# Revit family: HVAC_Heaters_Enertech_CTC-EcoHeat-400
name_source: partatom
category: Specialty Equipment
revit_build: Autodesk Revit 2017 (Build: 20190508_0315(x64)
units: mm (PartAtom-declared; Revit-internal decimal feet)

## family parameters
Always vertical = Yes
Cut with Voids When Loaded = No
OmniClass Number = 23.75.00.00
OmniClass Title = Climate Control (HVAC)
Part Type = Normal
Room Calculation Point = No
Round Connector Dimension = Use Diameter
Shared = No
Work Plane-Based = No

## types (12) — shared parameters
AssetType = Fixed
BIMObjectName = HVAC_Heaters_Enertech_CTC-EcoHeat-400
Brand = CTC
BrineSystem_Min_MaxPressure = 0.2-3.0 bar
Capacity = Fixed
Category = Heat pumps, Ground source
Color = White
ConvergoRefNr = 0091-1710-0011-SE
Description = CTC EcoHeat is a series of quiet, efficient on/off geothermal heat pumps with control touchscreen, hot water preparation and EnergyFlex, model 406-412, 6-12 kW, 230V-400V.
DurationUnit = Year
EnergyClass_HotWater_TapProfile = A/ L
HasProtectiveEarth = Yes
IP_Code = IP X1
IfcExportAs = IfcElectricalDeviceCommon
IfcExportType = HEATER
Manufacturer = Enertech AB
ManufacturerCountry = Sweden
ManufacturerName = Enertech AB
ManufacturerURL = https://ctc.se
Material = Steel/copper
MaxOperatingPressureHotWater = 10 bar
MaxOperatingPressureThermalStore = 3 bar
MinimumCeilingHeight = 1925 mm
NBSDescription = Air to water heat pumps
NBSReference = 90-40-40/320
Name = CTC-EcoHeat-400
NominalCurrent = 0 A
NominalDepth = 673 mm
NominalFrequencyRange = 50 Hz
NominalHeight = 1904 mm
NominalWidth = 596 mm
PhaseAngle = 0.00°
PowerFactor = 0 W
ProductInformation = CTC EcoHeat is a series of quiet, efficient on/off geothermal heat pumps with control touchscreen, hot water preparation and EnergyFlex, model 406-412, 6-12 kW, 230V-400V.
PumpMainMaterial = Stainless Steel
RefrigerantType = R407C
Revision = 4
Shape = Rectangular
Size = 673x596x1904 mm
Touchscreen = yes
UNSPSCCode = 40101806
URL = https://ctc-heating.com
Uniclass2 = Pr_40_70_65
Uniclass2015Description = Preparation catering equipment
Uniclass2015Reference = Pr_40_70_65
UsageCurrent = 0 A
Version = 1
VersionDate = 10/11/2020
WarrantyDurationUnit = Year
WaterVolumeHeathingSystem = 223 liters
WaterVolumeWaterSuply = 5.7 liters
zero-valued in all types: Cost

## per-type parameters (varying)
- CTC EcoHeat 406 - 400V3N: CO2Equivalent=3.370 tonnes; COP=4.57 kW; EANNumber=7333077000240; ElectricalDeviceNominalPower=9000 W; EnergyClassHeatingWithControl=A++/A+; EnergyClassHeatingWithoutControl=A++/A+; GroupFuse=10 A; HotTapWaterPerformance=173 liters; InPutPower=1.29 kW; MaxStartingCurrent=16.60 A; Model=CTC EcoHeat 406; ModelNumber=586610001; NominalVoltage=400 V; NumberOfPoles=3; OutputRangeIimmersionHeater=0.3-9.0 kW; RatedCurrent=12 A; RatedHeatOutputModerate=7 kW; RatedVoltage=1200 V; RefrigerantQuantity=1.9 kg; SCOPCold=4.3; SCOPModerate=4.3; SCOPWarm=4.1; Sound pressureLPA 1m=38 dB; SoundPowerLWA=43 dB; SpecifiedOutput=5.90 kW; Weight=273 kg
- CTC EcoHeat 408 - 400V3N: CO2Equivalent=3.370 tonnes; COP=4.58 kW; EANNumber=7333077000257; ElectricalDeviceNominalPower=9000 W; EnergyClassHeatingWithControl=A++/A++; EnergyClassHeatingWithoutControl=A++/A++; GroupFuse=10 A; HotTapWaterPerformance=173 liters; InPutPower=1.79 kW; MaxStartingCurrent=17.70 A; Model=CTC EcoHeat 408; ModelNumber=586610002; NominalVoltage=400 V; NumberOfPoles=3; OutputRangeIimmersionHeater=0.3-9.0 kW; RatedCurrent=13 A; RatedHeatOutputModerate=9 kW; RatedVoltage=1200 V; RefrigerantQuantity=1.9 kg; SCOPCold=4.2; SCOPModerate=4.2; SCOPWarm=4.1; Sound pressureLPA 1m=41 dB; SoundPowerLWA=46 dB; SpecifiedOutput=8.19 kW; Weight=274 kg
- CTC EcoHeat 410 - 400V3N: CO2Equivalent=3.370 tonnes; COP=4.60 kW; EANNumber=7333077000264; ElectricalDeviceNominalPower=9000 W; EnergyClassHeatingWithControl=A++/A++; EnergyClassHeatingWithoutControl=A++/A++; GroupFuse=10 A; HotTapWaterPerformance=173 liters; InPutPower=2.17 kW; MaxStartingCurrent=19.80 A; Model=CTC EcoHeat 410; ModelNumber=586610003; NominalVoltage=400 V; NumberOfPoles=3; OutputRangeIimmersionHeater=0.3-9.0 kW; RatedCurrent=13 A; RatedHeatOutputModerate=12 kW; RatedVoltage=1200 V; RefrigerantQuantity=1.9 kg; SCOPCold=4.2; SCOPModerate=4.1; SCOPWarm=4.0; Sound pressureLPA 1m=44 dB; SoundPowerLWA=49 dB; SpecifiedOutput=9.97 kW; Weight=278 kg
- CTC EcoHeat 412 - 400V3N: CO2Equivalent=4.080 tonnes; COP=4.60 kW; EANNumber=7333077000271; ElectricalDeviceNominalPower=9000 W; EnergyClassHeatingWithControl=A++/A++; EnergyClassHeatingWithoutControl=A++/A+; GroupFuse=16 A; HotTapWaterPerformance=173 liters; InPutPower=2.55 kW; MaxStartingCurrent=23.50 A; Model=CTC EcoHeat 412; ModelNumber=586610004; NominalVoltage=400 V; NumberOfPoles=3; OutputRangeIimmersionHeater=0.3-9.0 kW; RatedCurrent=14 A; RatedHeatOutputModerate=13 kW; RatedVoltage=1200 V; RefrigerantQuantity=2.3 kg; SCOPCold=4.1; SCOPModerate=4.1; SCOPWarm=4.0; Sound pressureLPA 1m=45 dB; SoundPowerLWA=50 dB; SpecifiedOutput=11.75 kW; Weight=291 kg
- CTC EcoHeat 406 - 230V1N: CO2Equivalent=3.370 tonnes; COP=4.57 kW; EANNumber=7333077000288; ElectricalDeviceNominalPower=9000 W; EnergyClassHeatingWithControl=A++/A+; EnergyClassHeatingWithoutControl=A++/A+; GroupFuse=16 A; HotTapWaterPerformance=173 liters; InPutPower=1.29 kW; MaxStartingCurrent=30 A; Model=CTC EcoHeat 406; ModelNumber=586611001; NominalVoltage=230 V; NumberOfPoles=1; OutputRangeIimmersionHeater=0.3-9.0 kW; RatedCurrent=52 A; RatedHeatOutputModerate=7 kW; RatedVoltage=230 V; RefrigerantQuantity=1.9 kg; SCOPCold=4.3; SCOPModerate=4.3; SCOPWarm=4.1; Sound pressureLPA 1m=38 dB; SoundPowerLWA=43 dB; SpecifiedOutput=5.90 kW; Weight=282 kg
- CTC EcoHeat 408 - 230V1N: CO2Equivalent=3.370 tonnes; COP=4.58 kW; EANNumber=7333077000295; ElectricalDeviceNominalPower=9000 W; EnergyClassHeatingWithControl=A++/A++; EnergyClassHeatingWithoutControl=A++/A++; GroupFuse=20 A; HotTapWaterPerformance=173 liters; InPutPower=1.79 kW; MaxStartingCurrent=30 A; Model=CTC EcoHeat 408; ModelNumber=586611002; NominalVoltage=230 V; NumberOfPoles=1; OutputRangeIimmersionHeater=0.3-9.0 kW; RatedCurrent=58 A; RatedHeatOutputModerate=9 kW; RatedVoltage=230 V; RefrigerantQuantity=1.9 kg; SCOPCold=4.2; SCOPModerate=4.2; SCOPWarm=4.1; Sound pressureLPA 1m=41 dB; SoundPowerLWA=46 dB; SpecifiedOutput=8.19 kW; Weight=270 kg
- CTC EcoHeat 410 - 230V1N: CO2Equivalent=3.370 tonnes; COP=4.60 kW; EANNumber=7333077000301; ElectricalDeviceNominalPower=9000 W; EnergyClassHeatingWithControl=A++/A++; EnergyClassHeatingWithoutControl=A++/A++; GroupFuse=25 A; HotTapWaterPerformance=173 liters; InPutPower=2.17 kW; MaxStartingCurrent=30 A; Model=CTC EcoHeat 410; ModelNumber=586611003; NominalVoltage=230 V; NumberOfPoles=1; OutputRangeIimmersionHeater=0.3-9.0 kW; RatedCurrent=60 A; RatedHeatOutputModerate=12 kW; RatedVoltage=230 V; RefrigerantQuantity=1.9 kg; SCOPCold=4.2; SCOPModerate=4.1; SCOPWarm=4.0; Sound pressureLPA 1m=44 dB; SoundPowerLWA=49 dB; SpecifiedOutput=9.97 kW; Weight=272 kg
- CTC EcoHeat 412 - 230V1N: CO2Equivalent=4.080 tonnes; COP=4.60 kW; EANNumber=7333077000318; ElectricalDeviceNominalPower=9000 W; EnergyClassHeatingWithControl=A++/A++; EnergyClassHeatingWithoutControl=A++/A+; GroupFuse=32 A; HotTapWaterPerformance=173 liters; InPutPower=2.55 kW; MaxStartingCurrent=30 A; Model=CTC EcoHeat 412; ModelNumber=586611004; NominalVoltage=230 V; NumberOfPoles=1; OutputRangeIimmersionHeater=0.3-9.0 kW; RatedCurrent=64 A; RatedHeatOutputModerate=13 kW; RatedVoltage=230 V; RefrigerantQuantity=2.3 kg; SCOPCold=4.1; SCOPModerate=4.1; SCOPWarm=4.0; Sound pressureLPA 1m=45 dB; SoundPowerLWA=50 dB; SpecifiedOutput=11.75 kW; Weight=279 kg
- CTC EcoHeat 412 - 230V3N: CO2Equivalent=4.080 tonnes; COP=4.60 kW; EANNumber=7333077000356; ElectricalDeviceNominalPower=7050 W; EnergyClassHeatingWithControl=A++/A++; EnergyClassHeatingWithoutControl=A++/A+; HotTapWaterPerformance=177 liters; InPutPower=2.55 kW; MaxStartingCurrent=30 A; Model=CTC EcoHeat 412; ModelNumber=586612004; NominalVoltage=230 V; NumberOfPoles=3; OutputRangeIimmersionHeater=1.02-7.05 kW; RatedCurrent=43 A; RatedHeatOutputModerate=13 kW; RatedVoltage=690 V; RefrigerantQuantity=2.3 kg; SCOPCold=4.1; SCOPModerate=4.1; SCOPWarm=4.0; Sound pressureLPA 1m=45 dB; SoundPowerLWA=50 dB; SpecifiedOutput=11.75 kW; Weight=279 kg
- CTC EcoHeat 406 - 230V3N: CO2Equivalent=3.370 tonnes; COP=4.57 kW; EANNumber=7333077000325; ElectricalDeviceNominalPower=7050 W; EnergyClassHeatingWithControl=A++/A+; EnergyClassHeatingWithoutControl=A++/A+; HotTapWaterPerformance=174 liters; InPutPower=1.29 kW; MaxStartingCurrent=30 A; Model=CTC EcoHeat 406; ModelNumber=586612001; NominalVoltage=230 V; NumberOfPoles=3; OutputRangeIimmersionHeater=1.02-7.05 kW; RatedCurrent=31 A; RatedHeatOutputModerate=7 kW; RatedVoltage=690 V; RefrigerantQuantity=1.9 kg; SCOPCold=4.3; SCOPModerate=4.3; SCOPWarm=4.1; Sound pressureLPA 1m=38 dB; SoundPowerLWA=43 dB; SpecifiedOutput=5.90 kW; Weight=282 kg
- CTC EcoHeat 408 - 230V3N: CO2Equivalent=3.370 tonnes; COP=4.58 kW; EANNumber=7333077000332; ElectricalDeviceNominalPower=7050 W; EnergyClassHeatingWithControl=A++/A++; EnergyClassHeatingWithoutControl=A++/A++; HotTapWaterPerformance=175 liters; InPutPower=1.79 kW; MaxStartingCurrent=30 A; Model=CTC EcoHeat 408; ModelNumber=586612002; NominalVoltage=230 V; NumberOfPoles=3; OutputRangeIimmersionHeater=1.02-7.05 kW; RatedCurrent=36 A; RatedHeatOutputModerate=9 kW; RatedVoltage=690 V; RefrigerantQuantity=1.9 kg; SCOPCold=4.2; SCOPModerate=4.2; SCOPWarm=4.1; Sound pressureLPA 1m=41 dB; SoundPowerLWA=46 dB; SpecifiedOutput=8.19 kW; Weight=270 kg
- CTC EcoHeat 410 - 230V3N: CO2Equivalent=3.370 tonnes; COP=4.60 kW; EANNumber=7333077000349; ElectricalDeviceNominalPower=7050 W; EnergyClassHeatingWithControl=A++/A++; EnergyClassHeatingWithoutControl=A++/A++; HotTapWaterPerformance=176 liters; InPutPower=2.17 kW; MaxStartingCurrent=30 A; Model=CTC EcoHeat 410; ModelNumber=586612003; NominalVoltage=230 V; NumberOfPoles=3; OutputRangeIimmersionHeater=1.02-7.05 kW; RatedCurrent=38 A; RatedHeatOutputModerate=12 kW; RatedVoltage=690 V; RefrigerantQuantity=1.9 kg; SCOPCold=4.2; SCOPModerate=4.1; SCOPWarm=4.0; Sound pressureLPA 1m=44 dB; SoundPowerLWA=49 dB; SpecifiedOutput=9.97 kW; Weight=272 kg

## geometry (parser evidence)
native form markers: Sweep x2
no freeform markers — native parametric forms only
